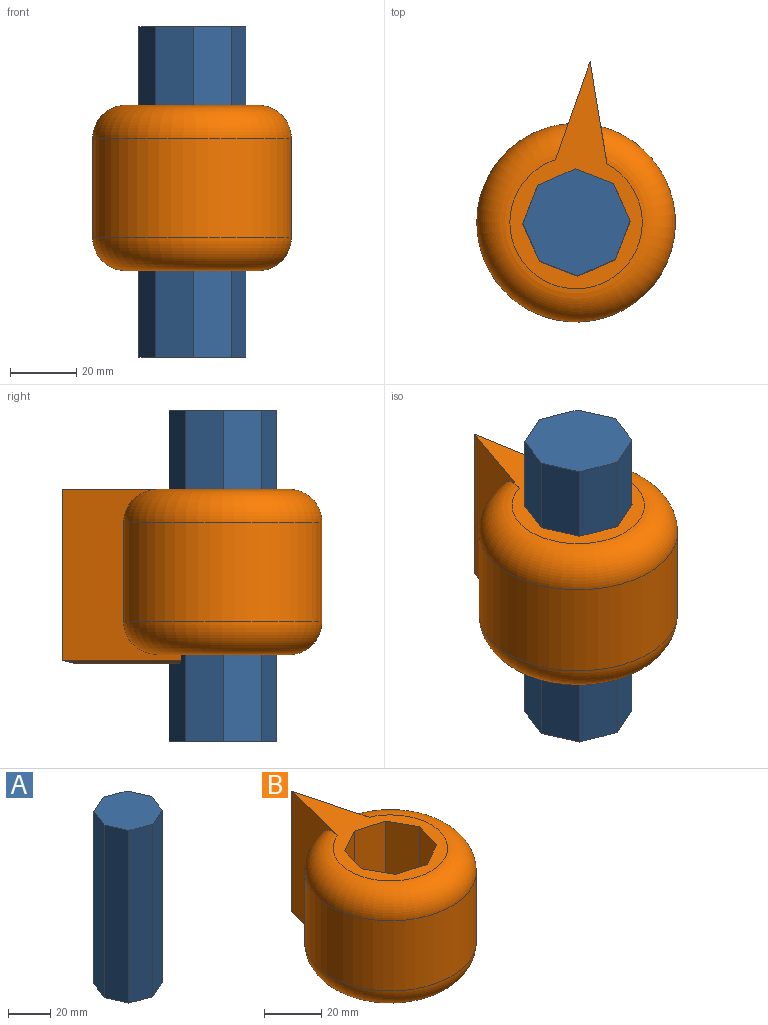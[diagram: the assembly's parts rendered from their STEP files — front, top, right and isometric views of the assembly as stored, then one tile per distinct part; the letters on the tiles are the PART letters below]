
ASSEMBLY  parts=2 mates=1
PART A: 10 faces, bbox 32.4x32.4x100 mm
  f0: plane 100x11.32mm, normal (0.41,-0.91,0), area 1238.5mm2, adj f1,f7,f8,f9
  f1: plane 100x11.56mm, normal (0.93,-0.36,0), area 1238.5mm2, adj f0,f2,f8,f9
  f2: plane 100x11.32mm, normal (0.91,0.41,0), area 1238.5mm2, adj f1,f3,f8,f9
  f3: plane 100x11.56mm, normal (0.36,0.93,0), area 1238.5mm2, adj f2,f4,f8,f9
  f4: plane 100x11.32mm, normal (-0.41,0.91,0), area 1238.5mm2, adj f3,f5,f8,f9
  f5: plane 100x11.56mm, normal (-0.93,0.36,0), area 1238.5mm2, adj f4,f6,f8,f9
  f6: plane 100x11.32mm, normal (-0.91,-0.41,0), area 1238.5mm2, adj f5,f7,f8,f9
  f7: plane 100x11.56mm, normal (-0.36,-0.93,0), area 1238.5mm2, adj f0,f6,f8,f9
  f8: plane 32.35x32.35mm, normal (0,0,1), area 740.6mm2, adj f0,f1,f2,f3,f4,f5,f6,f7
  f9: plane 32.35x32.35mm, normal (0,0,-1), area 740.6mm2, adj f0,f1,f2,f3,f4,f5,f6,f7
PART B: 18 faces, bbox 64.9x81.2x52.7 mm
  f0: cylinder r=30mm len=60mm, axis (0,0,-1), area 5357mm2, adj f3,f4,f8,f9
  f1: plane 40x38.4mm, normal (0,0,-1), area 426.9mm2, adj f3,f4,f8,f10,f11,f12,f13,f14
  f2: plane 68.73x40mm, normal (0,0,1), area 731.7mm2, adj f3,f4,f9,f10,f11,f12,f13,f14
  f3: plane 51.7x36.94mm, normal (-0.97,0.25,0), area 1101.1mm2, adj f0,f1,f2,f4,f7,f8,f9,f17
  f4: plane 51.7x35.74mm, normal (0.97,0.25,0), area 1099mm2, adj f0,f1,f2,f3,f6,f8,f9,f16
  f5: plane 32.27x16.44mm, normal (0,0,-1), area 234.4mm2, adj f6,f7,f16,f17
  f6: plane 35.74x9.23mm, normal (0.68,0.18,-0.71), area 49mm2, adj f4,f5,f7,f16
  f7: plane 36.94x9.54mm, normal (-0.68,0.18,-0.71), area 50.5mm2, adj f3,f5,f6,f17
  f8: torus R=20mm, axis (0,0,1), area 2412.8mm2, adj f0,f1,f3,f4
  f9: torus R=20mm, axis (0,0,1), area 2412.7mm2, adj f0,f2,f3,f4
  f10: plane 50x11.94mm, normal (-0.96,0.28,0), area 621.3mm2, adj f1,f2,f11,f15
  f11: plane 50x10.87mm, normal (-0.88,-0.48,0), area 621.3mm2, adj f1,f2,f10,f16
  f12: plane 50x11.94mm, normal (0.96,-0.28,0), area 621.3mm2, adj f1,f2,f13,f17
  f13: plane 50x10.87mm, normal (0.88,0.48,0), area 621.3mm2, adj f1,f2,f12,f14
  f14: plane 50x11.94mm, normal (0.28,0.96,0), area 621.3mm2, adj f1,f2,f13,f15
  f15: plane 50x10.87mm, normal (-0.48,0.88,0), area 621.3mm2, adj f1,f2,f10,f14
  f16: plane 52.7x11.94mm, normal (-0.28,-0.96,0), area 651.4mm2, adj f1,f2,f4,f5,f6,f11,f17
  f17: plane 52.7x10.87mm, normal (0.48,-0.88,0), area 644.9mm2, adj f1,f2,f3,f5,f7,f12,f16
PLACE A t=(0,0,82.4)mm
PLACE B rot(axis=(0,0,-1),5deg) t=(-0.12,-0.05,108.62)mm
MATE parallel B.f16 <-> A.f3  axis (-0.36,-0.93,0) through (5.37,13.95,132.4)mm
